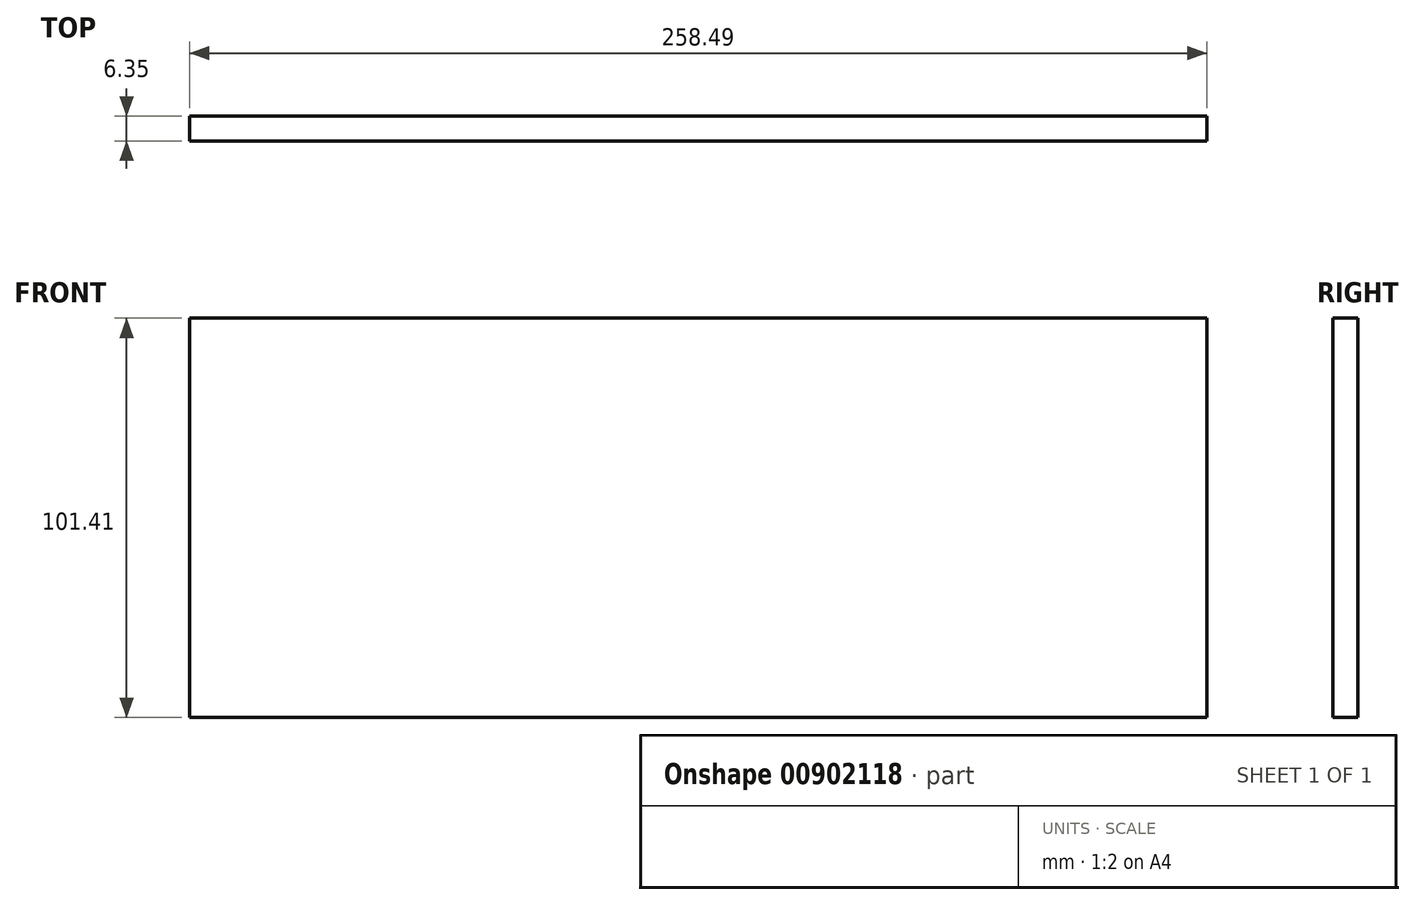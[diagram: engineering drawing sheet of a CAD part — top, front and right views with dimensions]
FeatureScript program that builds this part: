
annotation { "Feature Type Name" : "Feature", "Feature Type Description" : "" }
export const myFeature = defineFeature(function(context is Context, id is Id, definition is map)
    precondition{}
    {
        {
            var Q0;
            Q0=qCreatedBy(makeId("Front.planeOp"),FACE);
            var sketch = newSketch(context, id + "F0", { "sketchPlane" : qUnion([Q0])});
            skLineSegment(sketch, "E0.bottom", {"start": v(-172.7, 16.53) * mm, "end": v(85.8, 16.53) * mm});
            skLineSegment(sketch, "E0.top", {"start": v(-172.7, -84.88) * mm, "end": v(85.8, -84.88) * mm});
            skLineSegment(sketch, "E0.left", {"start": v(-172.7, 16.53) * mm, "end": v(-172.7, -84.88) * mm});
            skLineSegment(sketch, "E0.right", {"start": v(85.8, 16.53) * mm, "end": v(85.8, -84.88) * mm});
            skSolve(sketch);
        }
        {
            var Q0;
            Q0=makeQuery(id+"F0.imprint","IMPRINT",FACE,{"disambiguationData":[TD([[makeQuery(id+"F0.imprint","IMPRINT",EDGE,{"derivedFrom":sQuery(id+"F0.wireOp",EDGE,"E0.bottom")}),-1.0]])]});
            extrude(context, id + "F1", {"entities" : qUnion([Q0]), "depth" : 6.35 * mm, "offsetDistance" : 25.4 * mm});
        }
    });
